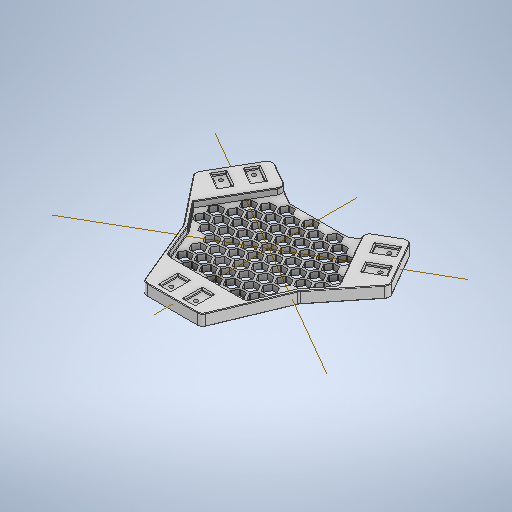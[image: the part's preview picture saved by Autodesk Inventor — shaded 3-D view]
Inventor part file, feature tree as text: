
AUTODESK INVENTOR PART (.ipt)
format: ipt  version: 2025 (Build 290162000, 162)  size: 1,532,416 bytes
history: native  units: in
note: dims shown in document units (in); Inventor stores cm internally (conversion verified against a paired STEP export)
features: extrude x6, fillet x5, sketch x4, projected_geometry x4, other x3, pattern_linear x1
ambient origin geometry x8: Origin, YZ Plane, XZ Plane, XY Plane, X Axis, Y Axis, Z Axis, Center Point
bodies: Solid1 (feature_tree)
feature tree (23):
  extrude  "Extrusion1"  Depth=3.937in
  extrude  "Extrusion2"  Depth=0.1969in
  sketch  "Sketch4"  dims[d4=0.1969in d5=0.0in d6=0.5197in]
  extrude  "Extrusion3"  TaperAngle=120.0deg  [1 undecoded]
  extrude  "Extrusion4"  Depth=1.9685in
  fillet  "Fillet3"  Radius=1.9685in
  fillet  "Fillet4"  Radius=0.1181in
  extrude  "Extrusion5"  Depth=0.0197in
  fillet  "Fillet6"  Radius=0.1969in
  fillet  "Fillet7"  Radius=2.3622in
  extrude  "Extrusion6"  Depth=1.1811in
  other  "Work Axis1"
  other  "Work Axis2"
  other  "Work Axis3"
  pattern_linear  "Rectangular Pattern1"  Spacing1=0.3937in  [1 undecoded]
  fillet  "Fillet8"  Radius=0.3937in
  sketch  "Sketch2"  dims[d2=2.0472in d3=3.937in]
  projected_geometry  "Projected Loop1"
  projected_geometry  "Projected Loop3"
  sketch  "Sketch5"  dims[d7=120.0deg d8=120.0deg]
  projected_geometry  "Projected Loop4"
  sketch  "Sketch6"  dims[d9=3.937in d10=1.9685in d11=1.9685in d12=0.1181in d13=0.1181in d14=0.1969in d15=0.0in d17=2.3622in d19=1.1811in d21=0.3937in d22=0.8327in d23=0.3937in d25=0.126in d26=0.3543in d27=0.5984in d28=0.3543in d29=0.5984in d30=0.3543in d31=0.5984in d32=0.3543in d33=0.5984in d34=0.3543in d35=0.5984in d36=0.3543in d37=0.5984in d38=0.2008in d39=0.2008in d40=0.2008in d41=0.2008in d42=0.2008in d43=0.2008in d44=0.0827in d45=0.0in d46=0.0in d47=0.0in d48=0.0394in d49=0.0197in d51=0.2441in d52=0.1575in d53=0.0in d56=1.9685in d57=0.3937in d58=0.3937in d59=0.1969in d60=0.0197in d61=0.3937in d62=1.0in d63=0.0in d64=4.3307in d66=0.4724in d67=3.937in d69=0.4724in d70=0.0in d71=0.0197in]
  projected_geometry  "Projected Loop5"
note: 2 required parameter values undecoded (feature->parameter linkage not recoverable at this tier; creation-order binding heuristic only, values carry confidence <= 0.55)
